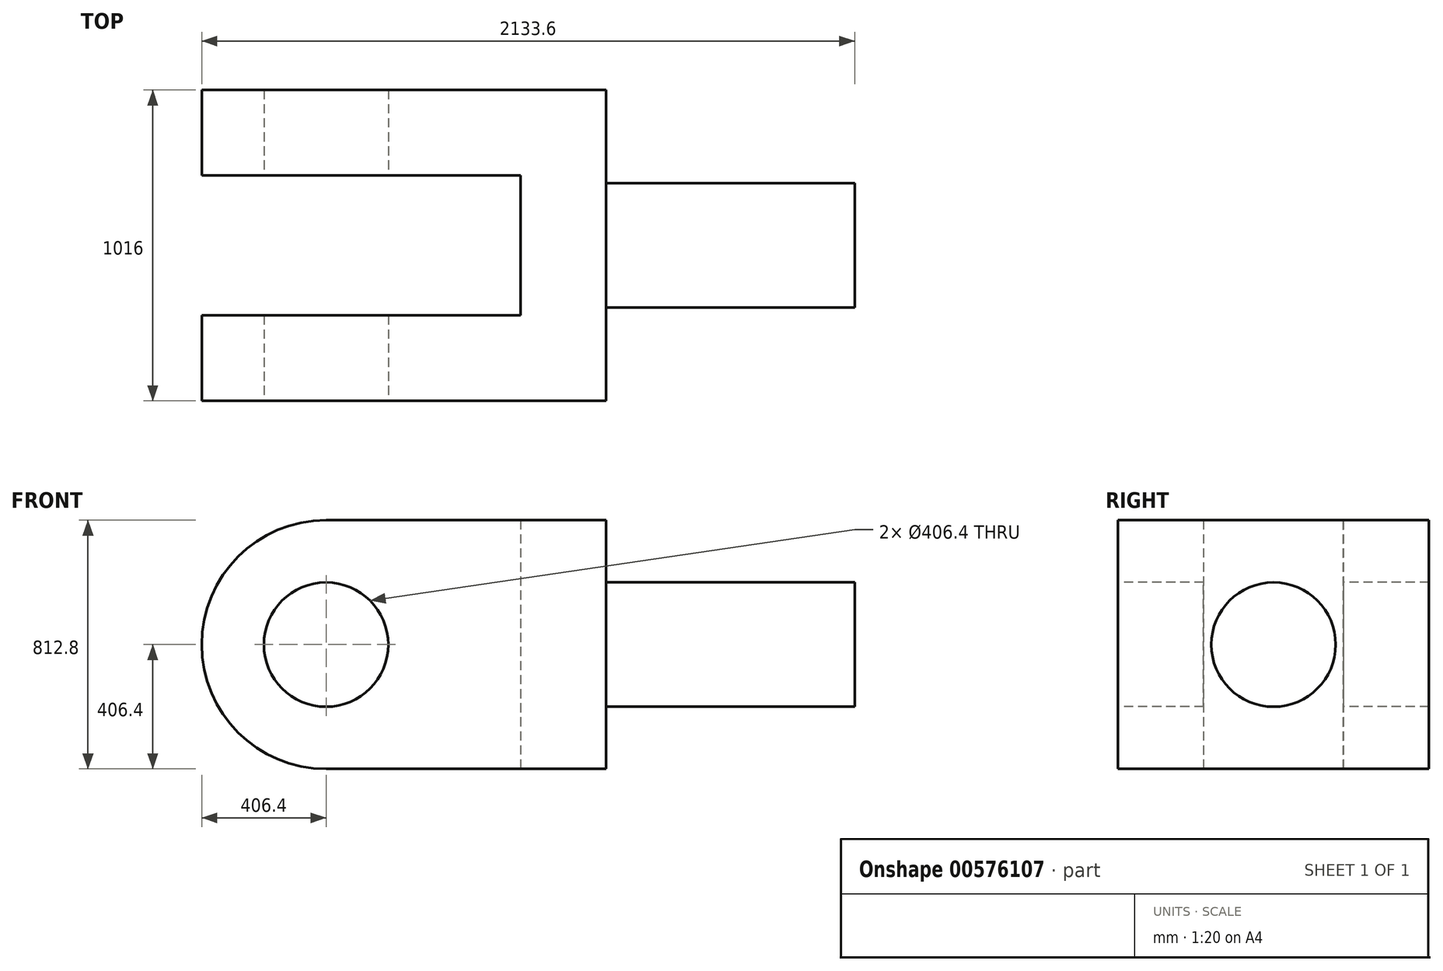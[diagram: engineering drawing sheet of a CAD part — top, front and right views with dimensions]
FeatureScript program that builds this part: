
annotation { "Feature Type Name" : "Feature", "Feature Type Description" : "" }
export const myFeature = defineFeature(function(context is Context, id is Id, definition is map)
    precondition{}
    {
        {
            var Q0;
            Q0=qCreatedBy(makeId("Top.planeOp"),FACE);
            var sketch = newSketch(context, id + "F0", { "sketchPlane" : qUnion([Q0])});
            skLineSegment(sketch, "E0", {"start": v(0, 0) * mm, "end": v(1320.8, 0) * mm});
            skLineSegment(sketch, "E1", {"start": v(1320.8, 0) * mm, "end": v(1320.8, 1016) * mm});
            skLineSegment(sketch, "E2", {"start": v(1320.8, 1016) * mm, "end": v(0, 1016) * mm});
            skLineSegment(sketch, "E3", {"start": v(0, 1016) * mm, "end": v(0, 736.6) * mm});
            skLineSegment(sketch, "E4", {"start": v(0, 736.6) * mm, "end": v(1041.4, 736.6) * mm});
            skLineSegment(sketch, "E5", {"start": v(1041.4, 736.6) * mm, "end": v(1041.4, 279.4) * mm});
            skLineSegment(sketch, "E6", {"start": v(1041.4, 279.4) * mm, "end": v(0, 279.4) * mm});
            skLineSegment(sketch, "E7", {"start": v(0, 279.4) * mm, "end": v(0, 0) * mm});
            skSolve(sketch);
        }
        {
            var Q0;
            Q0=makeQuery(id+"F0.imprint","IMPRINT",FACE,{"disambiguationData":[TD([[makeQuery(id+"F0.imprint","IMPRINT",EDGE,{"derivedFrom":sQuery(id+"F0.wireOp",EDGE,"E0")}),1.0]])]});
            extrude(context, id + "F1", {"entities" : qUnion([Q0]), "depth" : 812.8 * mm, "offsetDistance" : 25.4 * mm});
        }
        {
            var Q0;
            Q0=makeQuery(id+"F1.opExtrude","CAP_EDGE",EDGE,{"disambiguationData":[OSD([sQuery(id+"F0.wireOp",EDGE,"E7")])],"isStart":false});
            var Q1;
            Q1=makeQuery(id+"F1.opExtrude","CAP_EDGE",EDGE,{"disambiguationData":[OSD([sQuery(id+"F0.wireOp",EDGE,"E7")])],"isStart":true});
            var Q2;
            Q2=makeQuery(id+"F1.opExtrude","CAP_EDGE",EDGE,{"disambiguationData":[OSD([sQuery(id+"F0.wireOp",EDGE,"E3")])],"isStart":true});
            var Q3;
            Q3=makeQuery(id+"F1.opExtrude","CAP_EDGE",EDGE,{"disambiguationData":[OSD([sQuery(id+"F0.wireOp",EDGE,"E3")])],"isStart":false});
            fillet(context, id + "F2", {"entities" : qUnion([Q0, Q1, Q2, Q3]), "radius" : 406.4 * mm, "tangentPropagation" : true, "allowEdgeOverflow" : false});
        }
        {
            var Q0;
            Q0=makeQuery(id+"F1.opExtrude","SWEPT_FACE",FACE,{"disambiguationData":[OSD([sQuery(id+"F0.wireOp",EDGE,"E0")])]});
            var sketch = newSketch(context, id + "F3", { "sketchPlane" : qUnion([Q0])});
            skCircle(sketch, "E8", {"center": v(406.4, 406.4) * mm, "radius": 203.2 * mm});
            skSolve(sketch);
        }
        {
            var Q0;
            Q0=makeQuery(id+"F3.imprint","IMPRINT",FACE,{"disambiguationData":[TD([[makeQuery(id+"F3.imprint","IMPRINT",EDGE,{"derivedFrom":sQuery(id+"F3.wireOp",EDGE,"E8")}),1.0]])]});
            extrude(context, id + "F4", {"entities" : qUnion([Q0]), "operationType" : NewBodyOperationType.REMOVE, "endBound" : BoundingType.THROUGH_ALL, "oppositeDirection" : true, "depth" : 25.4 * mm, "offsetDistance" : 25.4 * mm});
        }
        {
            var Q0;
            Q0=makeQuery(id+"F1.opExtrude","SWEPT_FACE",FACE,{"disambiguationData":[OSD([sQuery(id+"F0.wireOp",EDGE,"E1")])]});
            var sketch = newSketch(context, id + "F5", { "sketchPlane" : qUnion([Q0])});
            skCircle(sketch, "E9", {"center": v(508, 406.4) * mm, "radius": 203.2 * mm});
            skPoint(sketch, "E9.centerSnap0", {"position": v(508, 0) * mm});
            skPoint(sketch, "E9.centerSnap1", {"position": v(1016, 406.4) * mm});
            skSolve(sketch);
        }
        {
            var Q0;
            Q0 = qSketchRegion(id + "F5", true);
            extrude(context, id + "F6", {"entities" : qUnion([Q0]), "operationType" : NewBodyOperationType.ADD, "depth" : 812.8 * mm, "offsetDistance" : 25.4 * mm});
        }
    });
